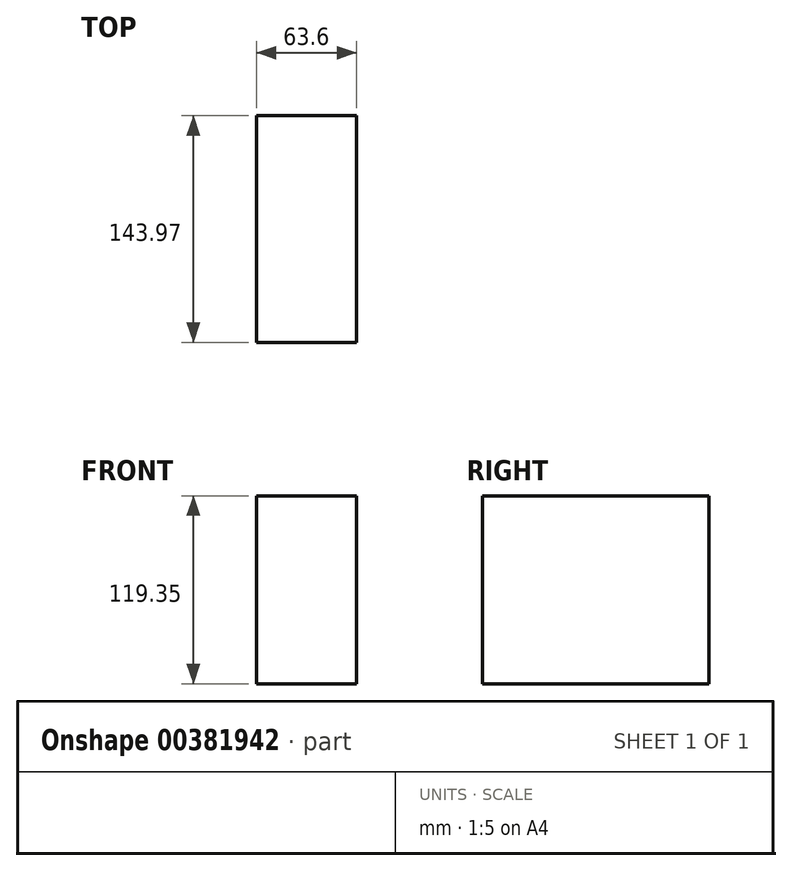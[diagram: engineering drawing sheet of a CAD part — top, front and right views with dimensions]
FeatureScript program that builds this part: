
annotation { "Feature Type Name" : "Feature", "Feature Type Description" : "" }
export const myFeature = defineFeature(function(context is Context, id is Id, definition is map)
    precondition{}
    {
        {
            var Q0;
            Q0=qCreatedBy(makeId("Top.planeOp"),FACE);
            var sketch = newSketch(context, id + "F0", { "sketchPlane" : qUnion([Q0])});
            skLineSegment(sketch, "E0.bottom", {"start": v(0, 0) * mm, "end": v(-63.6, 0) * mm});
            skLineSegment(sketch, "E0.top", {"start": v(0, -143.97) * mm, "end": v(-63.6, -143.97) * mm});
            skLineSegment(sketch, "E0.left", {"start": v(0, 0) * mm, "end": v(0, -143.97) * mm});
            skLineSegment(sketch, "E0.right", {"start": v(-63.6, 0) * mm, "end": v(-63.6, -143.97) * mm});
            skSolve(sketch);
        }
        {
            var Q0;
            Q0 = qSketchRegion(id + "F0", true);
            extrude(context, id + "F1", {"entities" : qUnion([Q0]), "depth" : 93.95 * mm, "hasSecondDirection" : true, "secondDirectionOppositeDirection" : true, "secondDirectionDepth" : 25.4 * mm});
        }
    });
